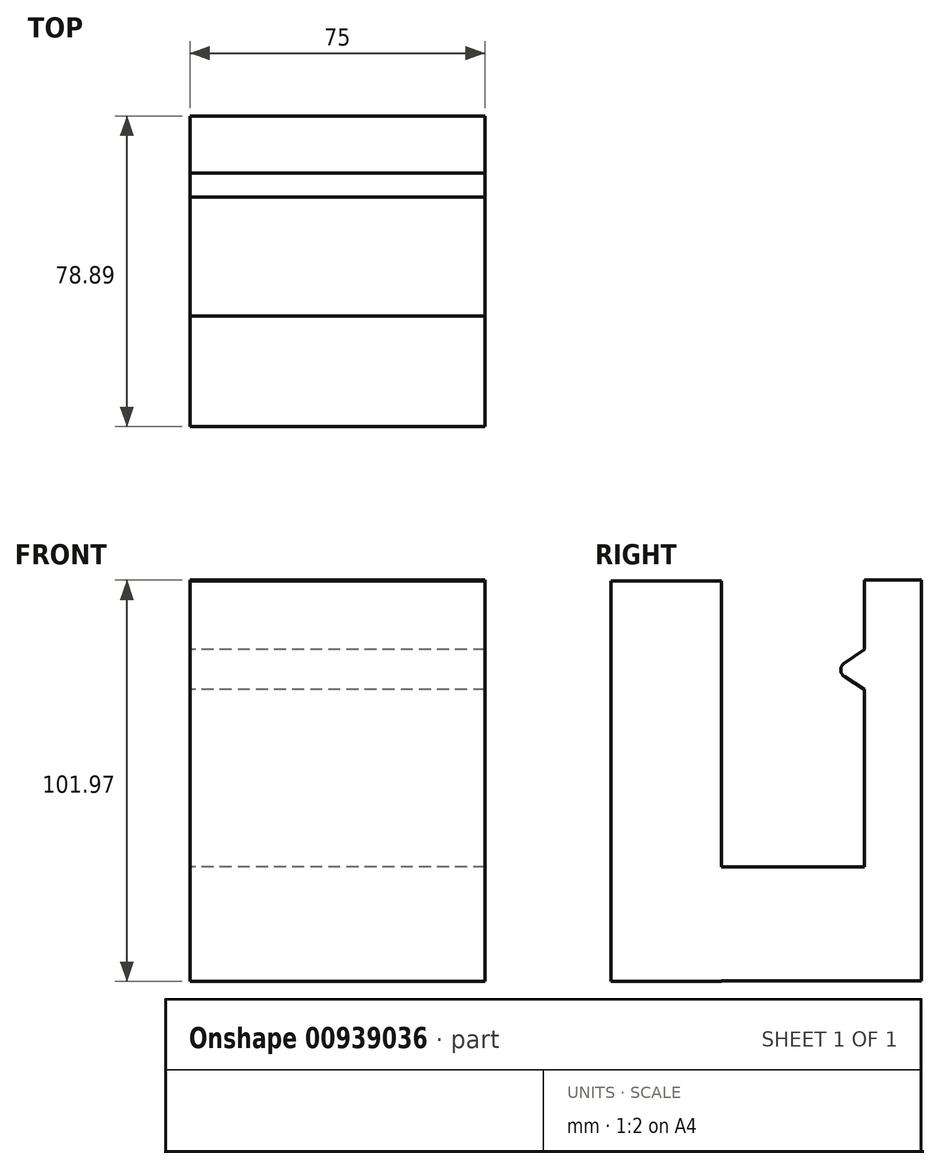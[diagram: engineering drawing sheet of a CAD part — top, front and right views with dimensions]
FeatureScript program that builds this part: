
annotation { "Feature Type Name" : "Feature", "Feature Type Description" : "" }
export const myFeature = defineFeature(function(context is Context, id is Id, definition is map)
    precondition{}
    {
        {
            var Q0;
            Q0=qCreatedBy(makeId("Right.planeOp"),FACE);
            var sketch = newSketch(context, id + "F0", { "sketchPlane" : qUnion([Q0])});
            skLineSegment(sketch, "E0.bottom", {"start": v(14.04, 50.85) * mm, "end": v(-14.04, 50.85) * mm});
            skLineSegment(sketch, "E0.top", {"start": v(14.04, -50.85) * mm, "end": v(-14.04, -50.85) * mm});
            skLineSegment(sketch, "E0.left", {"start": v(14.04, 50.85) * mm, "end": v(14.04, -50.85) * mm});
            skLineSegment(sketch, "E0.right", {"start": v(-14.04, 50.85) * mm, "end": v(-14.04, -50.85) * mm});
            skPoint(sketch, "E0.middle", {"position": v(0, 0) * mm});
            skLineSegment(sketch, "E1.bottom", {"start": v(14.04, -21.7) * mm, "end": v(64.85, -21.7) * mm});
            skLineSegment(sketch, "E1.top", {"start": v(14.04, -50.65) * mm, "end": v(64.85, -50.65) * mm});
            skLineSegment(sketch, "E1.left", {"start": v(14.04, -21.7) * mm, "end": v(14.04, -50.65) * mm});
            skLineSegment(sketch, "E1.right", {"start": v(64.85, -21.7) * mm, "end": v(64.85, -50.65) * mm});
            skLineSegment(sketch, "E2.bottom", {"start": v(64.85, -21.7) * mm, "end": v(50.36, -21.7) * mm});
            skLineSegment(sketch, "E2.top", {"start": v(64.85, 51.12) * mm, "end": v(50.36, 51.12) * mm});
            skLineSegment(sketch, "E2.left", {"start": v(64.85, -21.7) * mm, "end": v(64.85, 51.12) * mm});
            skLineSegment(sketch, "E2.right", {"start": v(50.36, -21.7) * mm, "end": v(50.36, 51.12) * mm});
            skLineSegment(sketch, "E3", {"start": v(50.36, 33.53) * mm, "end": v(45.17, 29.95) * mm});
            skLineSegment(sketch, "E4", {"start": v(45.22, 26.62) * mm, "end": v(50.36, 23.3) * mm});
            skPoint(sketch, "E5.visualSharp", {"position": v(42.7, 28.25) * mm});
            skArc(sketch, "E5.filletArc", {"start": v(45.17, 29.95) * mm, "mid": v(44.3, 28.27) * mm, "end": v(45.22, 26.62) * mm});
            skSolve(sketch);
        }
        {
            var Q0;
            {var subQ3=sQuery(id+"F0.wireOp",EDGE,"E0.bottom");Q0=makeQuery(id+"F0.imprint","IMPRINT",FACE,{"disambiguationData":[TD([[makeQuery(id+"F0.imprint","IMPRINT",EDGE,{"derivedFrom":subQ3}),1.0]])]});}
            var Q1;
            {var subQ5=sQuery(id+"F0.wireOp",EDGE,"E1.top");Q1=makeQuery(id+"F0.imprint","IMPRINT",FACE,{"disambiguationData":[TD([[makeQuery(id+"F0.imprint","IMPRINT",EDGE,{"derivedFrom":subQ5}),1.0]])]});}
            var Q2;
            {var subQ1=sQuery(id+"F0.wireOp",EDGE,"E2.top");Q2=makeQuery(id+"F0.imprint","IMPRINT",FACE,{"disambiguationData":[TD([[makeQuery(id+"F0.imprint","IMPRINT",EDGE,{"derivedFrom":subQ1}),1.0]])]});}
            var Q3;
            {var subQ0=sQuery(id+"F0.wireOp",EDGE,"E3");Q3=makeQuery(id+"F0.imprint","IMPRINT",FACE,{"disambiguationData":[TD([[makeQuery(id+"F0.imprint","IMPRINT",EDGE,{"derivedFrom":subQ0}),1.0]])]});}
            extrude(context, id + "F1", {"entities" : qUnion([Q0, Q1, Q2, Q3]), "endBound" : BoundingType.SYMMETRIC, "depth" : 75 * mm, "offsetDistance" : 25 * mm});
        }
    });
